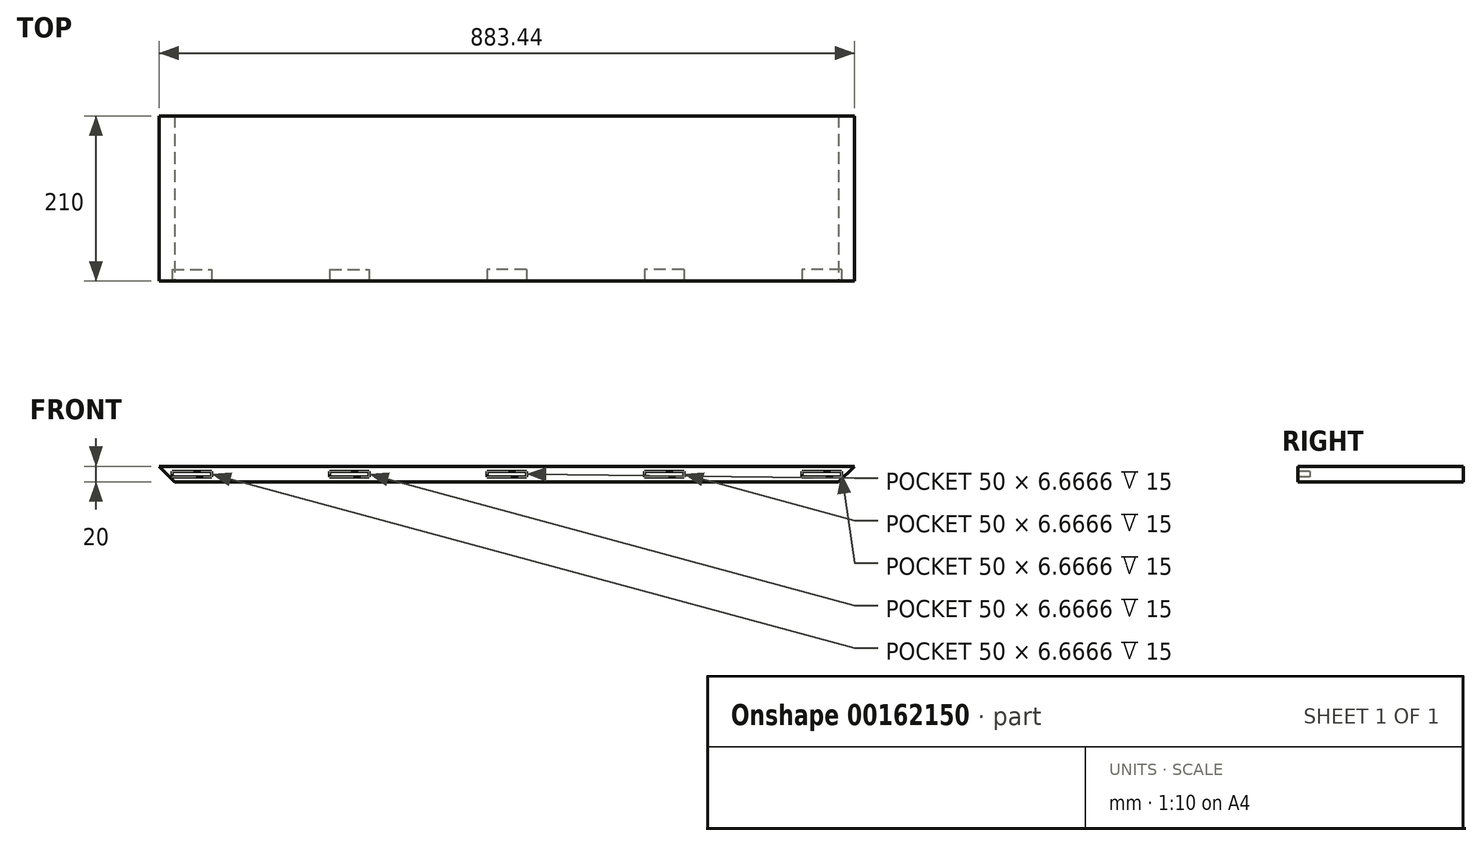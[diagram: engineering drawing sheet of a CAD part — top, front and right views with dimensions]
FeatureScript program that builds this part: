
annotation { "Feature Type Name" : "Feature", "Feature Type Description" : "" }
export const myFeature = defineFeature(function(context is Context, id is Id, definition is map)
    precondition{}
    {
        {
            assignVariable(context, id + "F0", {"name" : "t", "anyValue" : 20 * mm});
        }
        {
            var Q0;
            Q0=qCreatedBy(makeId("Top.planeOp"),FACE);
            var sketch = newSketch(context, id + "F1", { "sketchPlane" : qUnion([Q0])});
            skLineSegment(sketch, "E0.bottom", {"start": v(600, 105) * mm, "end": v(-600, 105) * mm});
            skLineSegment(sketch, "E0.top", {"start": v(600, -105) * mm, "end": v(-600, -105) * mm});
            skLineSegment(sketch, "E0.left", {"start": v(600, 105) * mm, "end": v(600, -105) * mm});
            skLineSegment(sketch, "E0.right", {"start": v(-600, 105) * mm, "end": v(-600, -105) * mm});
            skPoint(sketch, "E0.middle", {"position": v(0, 0) * mm});
            skSolve(sketch);
        }
        {
            var Q0;
            Q0=qSketchRegion(id+"F1",true);
            extrude(context, id + "F2", {"entities" : qUnion([Q0]), "endBound" : BoundingType.SYMMETRIC, "depth" : getVariable(context, 't')});
        }
        {
            var Q0;
            Q0=makeQuery(id+"F2.opExtrude","SWEPT_FACE",FACE,{"disambiguationData":[OSD([sQuery(id+"F1.wireOp",EDGE,"E0.top")])]});
            var sketch = newSketch(context, id + "F3", { "sketchPlane" : qUnion([Q0])});
            skLineSegment(sketch, "E1.bottom", {"start": v(25, 3.33) * mm, "end": v(-25, 3.33) * mm});
            skLineSegment(sketch, "E1.top", {"start": v(25, -3.33) * mm, "end": v(-25, -3.33) * mm});
            skLineSegment(sketch, "E1.left", {"start": v(25, 3.33) * mm, "end": v(25, -3.33) * mm});
            skLineSegment(sketch, "E1.right", {"start": v(-25, 3.33) * mm, "end": v(-25, -3.33) * mm});
            skPoint(sketch, "E1.middle", {"position": v(0, 0) * mm});
            skLineSegment(sketch, "E2.1.0.0", {"start": v(225, 3.33) * mm, "end": v(175, 3.33) * mm});
            skLineSegment(sketch, "E2.1.0.1", {"start": v(225, 3.33) * mm, "end": v(225, -3.33) * mm});
            skLineSegment(sketch, "E2.1.0.2", {"start": v(225, -3.33) * mm, "end": v(175, -3.33) * mm});
            skLineSegment(sketch, "E2.1.0.3", {"start": v(175, 3.33) * mm, "end": v(175, -3.33) * mm});
            skLineSegment(sketch, "E2.2.0.0", {"start": v(425, 3.33) * mm, "end": v(375, 3.33) * mm});
            skLineSegment(sketch, "E2.2.0.1", {"start": v(425, 3.33) * mm, "end": v(425, -3.33) * mm});
            skLineSegment(sketch, "E2.2.0.2", {"start": v(425, -3.33) * mm, "end": v(375, -3.33) * mm});
            skLineSegment(sketch, "E2.2.0.3", {"start": v(375, 3.33) * mm, "end": v(375, -3.33) * mm});
            skLineSegment(sketch, "E2.direction1", {"start": v(-25, 3.33) * mm, "end": v(175, 3.33) * mm, "construction": true});
            skLineSegment(sketch, "E3.MirrorCS", {"start": v(-175, 3.33) * mm, "end": v(-175, -3.33) * mm});
            skLineSegment(sketch, "E4.MirrorCS", {"start": v(-225, 3.33) * mm, "end": v(-175, 3.33) * mm});
            skLineSegment(sketch, "E5.MirrorCS", {"start": v(-225, -3.33) * mm, "end": v(-175, -3.33) * mm});
            skLineSegment(sketch, "E6.MirrorCS", {"start": v(-225, 3.33) * mm, "end": v(-225, -3.33) * mm});
            skLineSegment(sketch, "E7.MirrorCS", {"start": v(-425, 3.33) * mm, "end": v(-425, -3.33) * mm});
            skLineSegment(sketch, "E8.MirrorCS", {"start": v(-375, 3.33) * mm, "end": v(-375, -3.33) * mm});
            skLineSegment(sketch, "E9.MirrorCS", {"start": v(-425, 3.33) * mm, "end": v(-375, 3.33) * mm});
            skLineSegment(sketch, "E10.MirrorCS", {"start": v(-425, -3.33) * mm, "end": v(-375, -3.33) * mm});
            skLineSegment(sketch, "E11", {"start": v(0, 3.33) * mm, "end": v(0, 10) * mm, "construction": true});
            skSolve(sketch);
        }
        {
            var Q0;
            Q0=qSketchRegion(id+"F3",true);
            extrude(context, id + "F4", {"entities" : qUnion([Q0]), "operationType" : NewBodyOperationType.REMOVE, "oppositeDirection" : true, "depth" : getVariable(context, 't') / 2 + 5 * mm});
        }
        {
            var Q0;
            Q0=makeQuery(id+"F2.opExtrude","SWEPT_FACE",FACE,{"disambiguationData":[OSD([sQuery(id+"F1.wireOp",EDGE,"E0.top")])]});
            var sketch = newSketch(context, id + "F5", { "sketchPlane" : qUnion([Q0])});
            skLineSegment(sketch, "E12", {"start": v(-441.72, 10) * mm, "end": v(-421.72, -10) * mm});
            skLineSegment(sketch, "E13", {"start": v(-441.72, 10) * mm, "end": v(-600, 10) * mm});
            skLineSegment(sketch, "E14", {"start": v(-600, 10) * mm, "end": v(-600, -10) * mm});
            skLineSegment(sketch, "E15", {"start": v(-600, -10) * mm, "end": v(-421.72, -10) * mm});
            skLineSegment(sketch, "E16.MirrorCS", {"start": v(600, 10) * mm, "end": v(600, -10) * mm});
            skLineSegment(sketch, "E17.MirrorCS", {"start": v(441.72, 10) * mm, "end": v(600, 10) * mm});
            skLineSegment(sketch, "E18.MirrorCS", {"start": v(441.72, 10) * mm, "end": v(421.72, -10) * mm});
            skLineSegment(sketch, "E19.MirrorCS", {"start": v(600, -10) * mm, "end": v(421.72, -10) * mm});
            skSolve(sketch);
        }
        {
            var Q0;
            Q0 = qSketchRegion(id + "F5", true);
            extrude(context, id + "F6", {"entities" : qUnion([Q0]), "operationType" : NewBodyOperationType.REMOVE, "endBound" : BoundingType.THROUGH_ALL, "oppositeDirection" : true, "depth" : 25 * mm});
        }
    });
